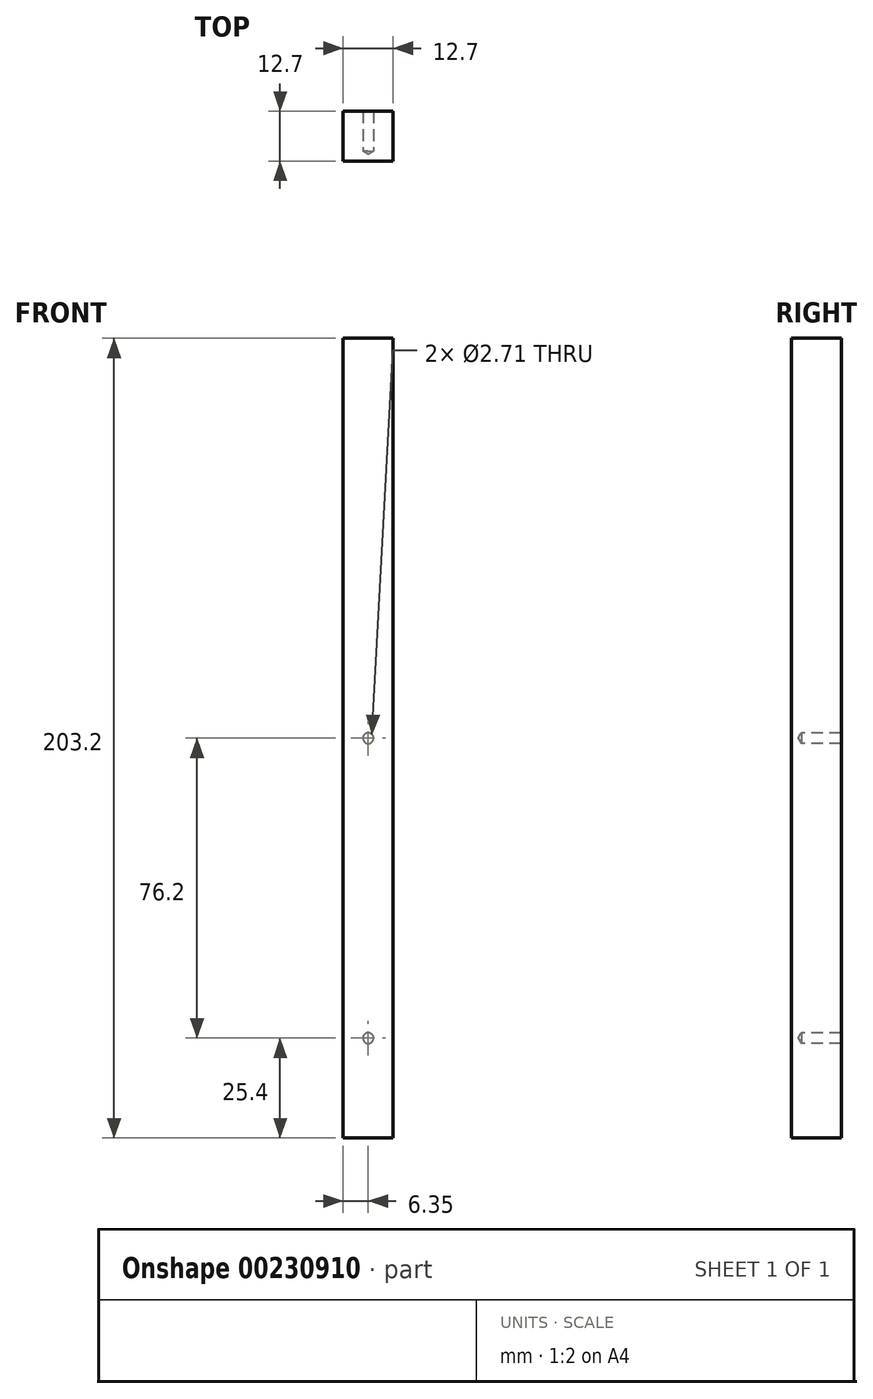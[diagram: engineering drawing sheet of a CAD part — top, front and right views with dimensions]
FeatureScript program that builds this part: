
annotation { "Feature Type Name" : "Feature", "Feature Type Description" : "" }
export const myFeature = defineFeature(function(context is Context, id is Id, definition is map)
    precondition{}
    {
        {
            var Q0;
            Q0=qCreatedBy(makeId("Top.planeOp"),FACE);
            var sketch = newSketch(context, id + "F0", { "sketchPlane" : qUnion([Q0])});
            skLineSegment(sketch, "E0.bottom", {"start": v(6.35, -6.35) * mm, "end": v(-6.35, -6.35) * mm});
            skLineSegment(sketch, "E0.top", {"start": v(6.35, 6.35) * mm, "end": v(-6.35, 6.35) * mm});
            skLineSegment(sketch, "E0.left", {"start": v(6.35, -6.35) * mm, "end": v(6.35, 6.35) * mm});
            skLineSegment(sketch, "E0.right", {"start": v(-6.35, -6.35) * mm, "end": v(-6.35, 6.35) * mm});
            skPoint(sketch, "E0.middle", {"position": v(0, 0) * mm});
            skSolve(sketch);
        }
        {
            var Q0;
            Q0 = qSketchRegion(id + "F0", true);
            extrude(context, id + "F1", {"entities" : qUnion([Q0]), "oppositeDirection" : true, "depth" : 203.2 * mm});
        }
        {
            var Q0;
            Q0=makeQuery(id+"F1.opExtrude","SWEPT_FACE",FACE,{"disambiguationData":[OSD([sQuery(id+"F0.wireOp",EDGE,"E0.top")])]});
            var sketch = newSketch(context, id + "F2", { "sketchPlane" : qUnion([Q0])});
            skLineSegment(sketch, "E1", {"start": v(0, -203.2) * mm, "end": v(0, 0) * mm, "construction": true});
            skPoint(sketch, "E2", {"position": v(0, -177.8) * mm});
            skPoint(sketch, "E3", {"position": v(0, -101.6) * mm});
            skSolve(sketch);
        }
        {
            var Q0;
            Q0=sQuery(id+"F2.wireOp",VERTEX,"E3");
            var Q1;
            Q1=sQuery(id+"F2.wireOp",VERTEX,"E2");
            var Q2;
            Q2=makeQuery(id+"F1.opExtrude","SWEPT_BODY",BODY,{"disambiguationData":[OSD([sQuery(id+"F0.wireOp",EDGE,"E0.bottom"),sQuery(id+"F0.wireOp",EDGE,"E0.top"),sQuery(id+"F0.wireOp",EDGE,"E0.left"),sQuery(id+"F0.wireOp",EDGE,"E0.right")])]});
            hole(context, id + "F3", {"style" : HoleStyle.SIMPLE, "endStyle" : HoleEndStyle.BLIND, "standardTappedOrClearance" : lookupTablePath({ "standard" : "ANSI", "engagement" : "75%", "pitch" : "32 tpi", "size" : "#6", "type" : "Tapped" }), "standardBlindInLast" : lookupTablePath({ "standard" : "ANSI", "engagement" : "75%", "pitch" : "32 tpi", "size" : "#6", "type" : "Tapped" }), "holeDiameter" : 2.7 * mm, "holeDepth" : 10.16 * mm, "locations" : qUnion([Q0, Q1]), "scope" : qUnion([Q2]), "tappedDepth" : 12.7 * mm, "tapClearance" : 3, "majorDiameter" : 3.5 * mm});
        }
    });
